# Revit family: 1116A_LightHAWK2_LHUS
name_source: partatom
category: Communication Devices
units: mm (PartAtom-declared; Revit-internal decimal feet)

## family parameters
Cut with Voids When Loaded = No
Host = Face
Maintain Annotation Orientation = No
OmniClass Number = 23.85.80.11.27
OmniClass Title = Lighting Controls
Part Type = Normal
Room Calculation Point = No
Round Connector Dimension = Use Diameter
Shared = Yes

## types (1)
- 1116A_LightHAWK2_LHUS
    Assembly Code = D5090
    Black = Paint -  Carbon Black
    Default Elevation = 48 "
    Description = The LightHAWK®2 Ultrasonic Wall Switch Sensor uses ultrasonic (US)
technology for detecting minor movement in areas with line-ofsight
obstacles such as cubicles and stalls. Ultrasonic technology is
volumetric in nature, its coverage pattern can adapt itself to fill oddly
shaped spaces such as alcoves, recesses, and nooks. This sensor has a
coverage area of up to 400 square feet and 180° of detection
    Features = Digital Ultrasonic (US) sensor 
IntelliDAPT self-adaptive technology—no manual adjustment required 
Dual circuit has isolated relays 
Occupancy (auto-on) and Vacancy (manual-on) operating modes 
Available with or without Neutral 
400 square-foot, 180° coverage area 
120/277VAC operation 
No minimum load requirement 
Zero Arc Point Switching 
Five-year limited warranty 
120-277VAC and 347VAC models 
Low voltage device: 24VDC
    Height = 4.5 "
    Manufacturer = NX Lighting Controls
    Model = Wall Switch Occupancy Sensors
    Type Comments = LightHAWK®2 Ultrasonic Wall Switch Sensor
    URL = https://www.currentlighting.com
    Warranty = 5-Years Warranty
    White = Paint - Matte White
    Width = 2.75 "

## geometry (parser evidence)
native form markers: Sweep x2
no freeform markers — native parametric forms only
